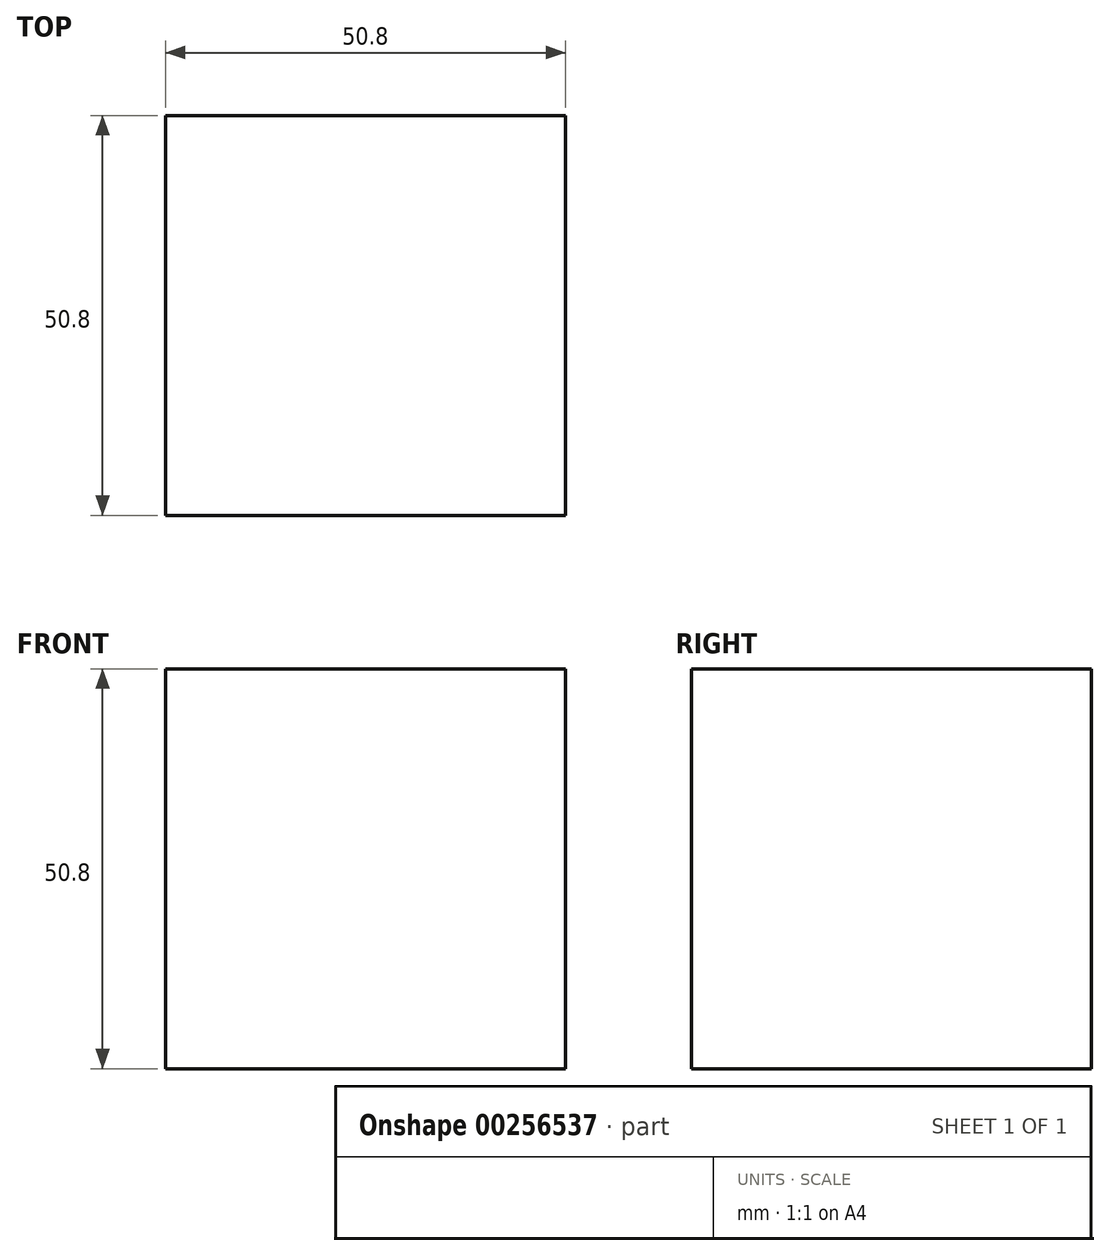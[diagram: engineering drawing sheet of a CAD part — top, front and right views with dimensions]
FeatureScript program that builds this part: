
annotation { "Feature Type Name" : "Feature", "Feature Type Description" : "" }
export const myFeature = defineFeature(function(context is Context, id is Id, definition is map)
    precondition{}
    {
        {
            var Q0;
            Q0=qCreatedBy(makeId("Top.planeOp"),FACE);
            var sketch = newSketch(context, id + "F0", { "sketchPlane" : qUnion([Q0])});
            skLineSegment(sketch, "E0.bottom", {"start": v(-25.4, 25.4) * mm, "end": v(25.4, 25.4) * mm});
            skLineSegment(sketch, "E0.top", {"start": v(-25.4, -25.4) * mm, "end": v(25.4, -25.4) * mm});
            skLineSegment(sketch, "E0.left", {"start": v(-25.4, 25.4) * mm, "end": v(-25.4, -25.4) * mm});
            skLineSegment(sketch, "E0.right", {"start": v(25.4, 25.4) * mm, "end": v(25.4, -25.4) * mm});
            skLineSegment(sketch, "E1", {"start": v(0, 25.4) * mm, "end": v(0, 0) * mm, "construction": true});
            skSolve(sketch);
        }
        {
            var Q0;
            Q0=makeQuery(id+"F0.imprint","IMPRINT",FACE,{"disambiguationData":[TD([[makeQuery(id+"F0.imprint","IMPRINT",EDGE,{"derivedFrom":sQuery(id+"F0.wireOp",EDGE,"E0.bottom")}),-1.0]])]});
            extrude(context, id + "F1", {"entities" : qUnion([Q0]), "depth" : 50.8 * mm});
        }
    });
